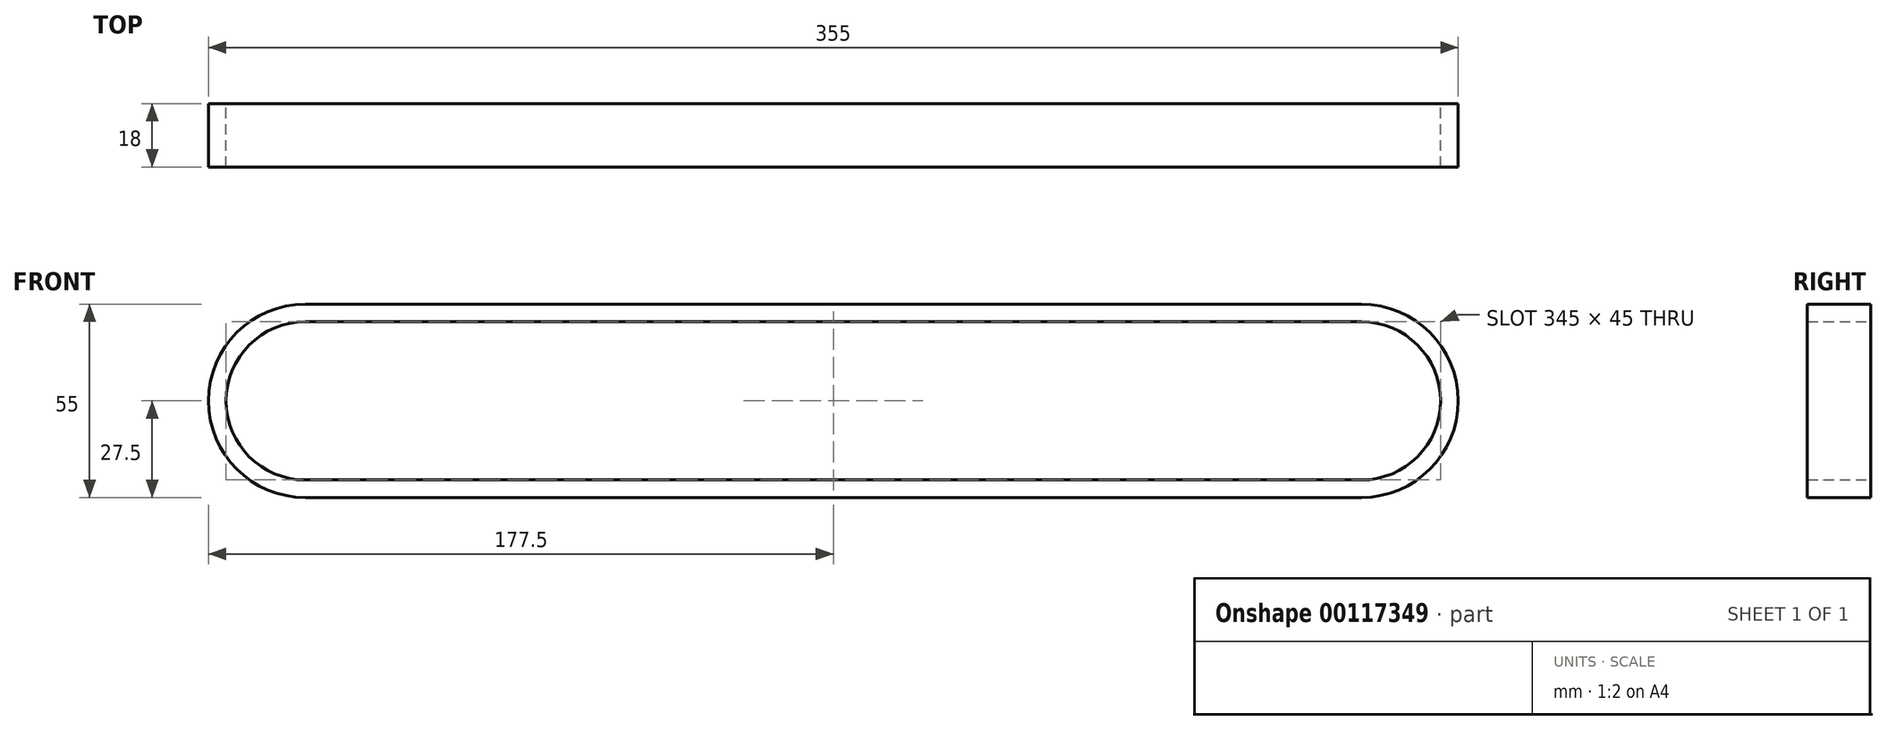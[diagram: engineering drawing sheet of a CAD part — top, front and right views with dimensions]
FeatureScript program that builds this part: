
annotation { "Feature Type Name" : "Feature", "Feature Type Description" : "" }
export const myFeature = defineFeature(function(context is Context, id is Id, definition is map)
    precondition{}
    {
        {
            var Q0;
            Q0=qCreatedBy(makeId("Front.planeOp"),FACE);
            var sketch = newSketch(context, id + "F0", { "sketchPlane" : qUnion([Q0])});
            skArc(sketch, "E0", {"start": v(0, -22.5) * mm, "mid": v(22.5, 0) * mm, "end": v(0, 22.5) * mm});
            skArc(sketch, "E1", {"start": v(-300, 22.5) * mm, "mid": v(-322.5, 0) * mm, "end": v(-300, -22.5) * mm});
            skLineSegment(sketch, "E2", {"start": v(-300, 22.5) * mm, "end": v(0, 22.5) * mm});
            skLineSegment(sketch, "E3", {"start": v(-300, -22.5) * mm, "end": v(0, -22.5) * mm});
            skLineSegment(sketch, "E4.0", {"start": v(-300, 27.5) * mm, "end": v(0, 27.5) * mm});
            skArc(sketch, "E4.1", {"start": v(-300, 27.5) * mm, "mid": v(-327.5, 0) * mm, "end": v(-300, -27.5) * mm});
            skLineSegment(sketch, "E4.2", {"start": v(-300, -27.5) * mm, "end": v(0, -27.5) * mm});
            skArc(sketch, "E4.3", {"start": v(0, -27.5) * mm, "mid": v(27.5, 0) * mm, "end": v(0, 27.5) * mm});
            skSolve(sketch);
        }
        {
            var Q0;
            Q0 = qSketchRegion(id + "F0", true);
            extrude(context, id + "F1", {"entities" : qUnion([Q0]), "depth" : 18 * mm});
        }
    });
